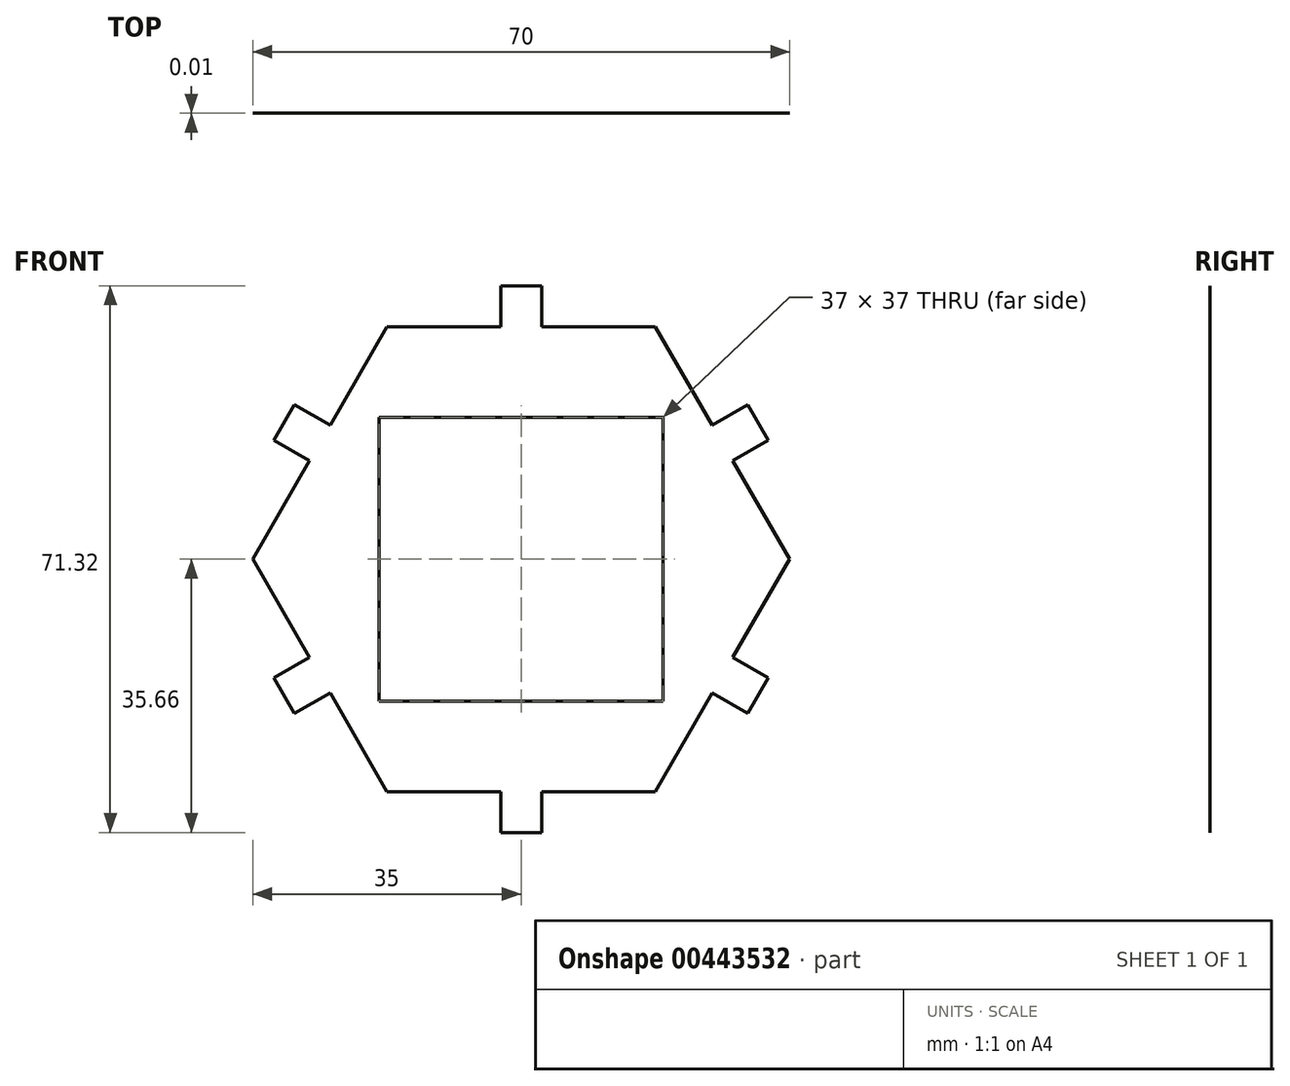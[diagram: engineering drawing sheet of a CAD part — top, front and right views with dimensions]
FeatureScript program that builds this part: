
annotation { "Feature Type Name" : "Feature", "Feature Type Description" : "" }
export const myFeature = defineFeature(function(context is Context, id is Id, definition is map)
    precondition{}
    {
        {
            var Q0;
            Q0=qCreatedBy(makeId("Front.planeOp"),FACE);
            var sketch = newSketch(context, id + "F0", { "sketchPlane" : qUnion([Q0])});
            skCircle(sketch, "E0.cCircle", {"center": v(0, 0) * mm, "radius": 30.31 * mm, "construction": true});
            skLineSegment(sketch, "E0.0", {"start": v(35, 0) * mm, "end": v(17.5, -30.31) * mm});
            skLineSegment(sketch, "E0.1", {"start": v(17.5, -30.31) * mm, "end": v(-17.5, -30.31) * mm});
            skLineSegment(sketch, "E0.2", {"start": v(-17.5, -30.31) * mm, "end": v(-35, 0) * mm});
            skLineSegment(sketch, "E0.3", {"start": v(-35, 0) * mm, "end": v(-17.5, 30.31) * mm});
            skLineSegment(sketch, "E0.4", {"start": v(-17.5, 30.31) * mm, "end": v(17.5, 30.31) * mm});
            skLineSegment(sketch, "E0.5", {"start": v(17.5, 30.31) * mm, "end": v(35, 0) * mm});
            skPoint(sketch, "E0.0.midPoint", {"position": v(26.25, -15.16) * mm});
            skSolve(sketch);
        }
        {
            var Q0;
            Q0 = qSketchRegion(id + "F0", true);
            extrude(context, id + "F1", {"entities" : qUnion([Q0]), "depth" : 1 / 101.6 * mm});
        }
        {
            var Q0;
            Q0=makeQuery(id+"F1.opExtrude","CAP_FACE",FACE,{"disambiguationData":[OSD([sQuery(id+"F0.wireOp",EDGE,"E0.0"),sQuery(id+"F0.wireOp",EDGE,"E0.1"),sQuery(id+"F0.wireOp",EDGE,"E0.2"),sQuery(id+"F0.wireOp",EDGE,"E0.3"),sQuery(id+"F0.wireOp",EDGE,"E0.4"),sQuery(id+"F0.wireOp",EDGE,"E0.5")])],"isStart":false});
            var sketch = newSketch(context, id + "F2", { "sketchPlane" : qUnion([Q0])});
            skLineSegment(sketch, "E1.bottom", {"start": v(-2.67, 30.31) * mm, "end": v(2.68, 30.31) * mm});
            skLineSegment(sketch, "E1.top", {"start": v(-2.67, 35.66) * mm, "end": v(2.67, 35.66) * mm});
            skLineSegment(sketch, "E1.left", {"start": v(-2.67, 30.31) * mm, "end": v(-2.67, 35.66) * mm});
            skLineSegment(sketch, "E1.right", {"start": v(2.68, 30.31) * mm, "end": v(2.68, 35.66) * mm});
            skLineSegment(sketch, "E2.bottom", {"start": v(-2.67, -30.31) * mm, "end": v(2.68, -30.31) * mm});
            skLineSegment(sketch, "E2.top", {"start": v(-2.67, -35.66) * mm, "end": v(2.68, -35.66) * mm});
            skLineSegment(sketch, "E2.left", {"start": v(-2.67, -30.31) * mm, "end": v(-2.67, -35.66) * mm});
            skLineSegment(sketch, "E2.right", {"start": v(2.68, -30.31) * mm, "end": v(2.68, -35.66) * mm});
            skPoint(sketch, "E3", {"position": v(0, 30.31) * mm});
            skPoint(sketch, "E4", {"position": v(0, -30.31) * mm});
            skLineSegment(sketch, "E5", {"start": v(24.91, 17.47) * mm, "end": v(27.59, 12.84) * mm});
            skLineSegment(sketch, "E6", {"start": v(27.59, 12.84) * mm, "end": v(32.22, 15.51) * mm});
            skLineSegment(sketch, "E7", {"start": v(32.22, 15.51) * mm, "end": v(29.55, 20.15) * mm});
            skLineSegment(sketch, "E8", {"start": v(29.55, 20.15) * mm, "end": v(24.91, 17.47) * mm});
            skPoint(sketch, "E9", {"position": v(26.25, 15.16) * mm});
            skPoint(sketch, "E10", {"position": v(-26.25, 15.16) * mm});
            skPoint(sketch, "E11", {"position": v(26.25, -15.16) * mm});
            skLineSegment(sketch, "E12", {"start": v(-27.59, 12.84) * mm, "end": v(-24.91, 17.47) * mm});
            skLineSegment(sketch, "E13", {"start": v(-27.59, -12.84) * mm, "end": v(-24.91, -17.47) * mm});
            skLineSegment(sketch, "E14", {"start": v(-24.91, -17.47) * mm, "end": v(-29.55, -20.15) * mm});
            skLineSegment(sketch, "E15", {"start": v(-29.55, -20.15) * mm, "end": v(-32.22, -15.51) * mm});
            skLineSegment(sketch, "E16", {"start": v(-32.22, -15.51) * mm, "end": v(-27.59, -12.84) * mm});
            skPoint(sketch, "E17", {"position": v(-26.25, -15.16) * mm});
            skLineSegment(sketch, "E18", {"start": v(-27.59, 12.84) * mm, "end": v(-32.22, 15.51) * mm});
            skLineSegment(sketch, "E19", {"start": v(-32.22, 15.51) * mm, "end": v(-29.55, 20.15) * mm});
            skLineSegment(sketch, "E20", {"start": v(-29.55, 20.15) * mm, "end": v(-24.91, 17.47) * mm});
            skLineSegment(sketch, "E21", {"start": v(24.91, -17.47) * mm, "end": v(27.59, -12.84) * mm});
            skLineSegment(sketch, "E22", {"start": v(27.59, -12.84) * mm, "end": v(32.22, -15.51) * mm});
            skLineSegment(sketch, "E23", {"start": v(32.22, -15.51) * mm, "end": v(29.55, -20.15) * mm});
            skLineSegment(sketch, "E24", {"start": v(29.55, -20.15) * mm, "end": v(24.91, -17.47) * mm});
            skSolve(sketch);
        }
        {
            var Q0;
            Q0 = qSketchRegion(id + "F2", true);
            extrude(context, id + "F3", {"entities" : qUnion([Q0]), "operationType" : NewBodyOperationType.ADD, "oppositeDirection" : true, "depth" : 1 / 101.6 * mm});
        }
        {
            var Q0;
            Q0=makeQuery(id+"F3.boolean.opBoolean","MERGE",FACE,{"derivedFrom":[makeQuery(id+"F1.opExtrude","CAP_FACE",FACE,{"disambiguationData":[OSD([sQuery(id+"F0.wireOp",EDGE,"E0.0"),sQuery(id+"F0.wireOp",EDGE,"E0.1"),sQuery(id+"F0.wireOp",EDGE,"E0.2"),sQuery(id+"F0.wireOp",EDGE,"E0.3"),sQuery(id+"F0.wireOp",EDGE,"E0.4"),sQuery(id+"F0.wireOp",EDGE,"E0.5")])],"isStart":false}),makeQuery(id+"F3.opExtrude","CAP_FACE",FACE,{"disambiguationData":[OSD([sQuery(id+"F2.wireOp",EDGE,"E1.bottom"),sQuery(id+"F2.wireOp",EDGE,"E1.top"),sQuery(id+"F2.wireOp",EDGE,"E1.left"),sQuery(id+"F2.wireOp",EDGE,"E1.right")])],"isStart":true}),makeQuery(id+"F3.opExtrude","CAP_FACE",FACE,{"disambiguationData":[OSD([sQuery(id+"F2.wireOp",EDGE,"E2.bottom"),sQuery(id+"F2.wireOp",EDGE,"E2.top"),sQuery(id+"F2.wireOp",EDGE,"E2.left"),sQuery(id+"F2.wireOp",EDGE,"E2.right")])],"isStart":true}),makeQuery(id+"F3.opExtrude","CAP_FACE",FACE,{"disambiguationData":[OSD([sQuery(id+"F2.wireOp",EDGE,"E5"),sQuery(id+"F2.wireOp",EDGE,"E6"),sQuery(id+"F2.wireOp",EDGE,"E7"),sQuery(id+"F2.wireOp",EDGE,"E8")])],"isStart":true}),makeQuery(id+"F3.opExtrude","CAP_FACE",FACE,{"disambiguationData":[OSD([sQuery(id+"F2.wireOp",EDGE,"E12"),sQuery(id+"F2.wireOp",EDGE,"E18"),sQuery(id+"F2.wireOp",EDGE,"E19"),sQuery(id+"F2.wireOp",EDGE,"E20")])],"isStart":true}),makeQuery(id+"F3.opExtrude","CAP_FACE",FACE,{"disambiguationData":[OSD([sQuery(id+"F2.wireOp",EDGE,"E13"),sQuery(id+"F2.wireOp",EDGE,"E14"),sQuery(id+"F2.wireOp",EDGE,"E15"),sQuery(id+"F2.wireOp",EDGE,"E16")])],"isStart":true}),makeQuery(id+"F3.opExtrude","CAP_FACE",FACE,{"disambiguationData":[OSD([sQuery(id+"F2.wireOp",EDGE,"E21"),sQuery(id+"F2.wireOp",EDGE,"E22"),sQuery(id+"F2.wireOp",EDGE,"E23"),sQuery(id+"F2.wireOp",EDGE,"E24")])],"isStart":true})]});
            var sketch = newSketch(context, id + "F4", { "sketchPlane" : qUnion([Q0])});
            skLineSegment(sketch, "E25.bottom", {"start": v(-18.5, 18.5) * mm, "end": v(18.5, 18.5) * mm});
            skLineSegment(sketch, "E25.top", {"start": v(-18.5, -18.5) * mm, "end": v(18.5, -18.5) * mm});
            skLineSegment(sketch, "E25.left", {"start": v(-18.5, 18.5) * mm, "end": v(-18.5, -18.5) * mm});
            skLineSegment(sketch, "E25.right", {"start": v(18.5, 18.5) * mm, "end": v(18.5, -18.5) * mm});
            skPoint(sketch, "E26", {"position": v(18.5, 0) * mm});
            skPoint(sketch, "E27", {"position": v(-18.5, 0) * mm});
            skSolve(sketch);
        }
        {
            var Q0;
            Q0 = qSketchRegion(id + "F4", true);
            extrude(context, id + "F5", {"entities" : qUnion([Q0]), "operationType" : NewBodyOperationType.REMOVE, "oppositeDirection" : true, "depth" : 25 * mm});
        }
    });
